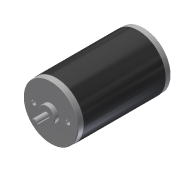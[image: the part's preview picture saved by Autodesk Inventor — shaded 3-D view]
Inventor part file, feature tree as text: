
AUTODESK INVENTOR PART (.ipt)
format: ipt  version: 2013 (Build 170138000, 138)  size: 130,048 bytes
history: native  units: in
note: dims shown in document units (in); Inventor stores cm internally (conversion verified against a paired STEP export)
features: chamfer x1, imported_body x1
ambient origin geometry x8: Origin, YZ Plane, XZ Plane, XY Plane, X Axis, Y Axis, Z Axis, Center Point
feature tree (2):
  chamfer  "Chamfer1"  [1 undecoded]
  imported_body  "Base1"
note: 1 required parameter value undecoded (feature->parameter linkage not recoverable at this tier; creation-order binding heuristic only, values carry confidence <= 0.55)
